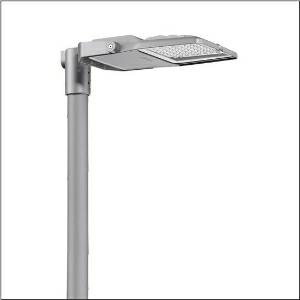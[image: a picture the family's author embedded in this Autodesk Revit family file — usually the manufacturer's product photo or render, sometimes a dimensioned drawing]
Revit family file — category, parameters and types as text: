
# Revit family: floodlight_fl_21_mini___pl33t_5xa7776c2f3a_ca81
name_source: partatom
category: Lighting Fixtures
units: mm (PartAtom-declared; Revit-internal decimal feet)

## family parameters
Cut with Voids When Loaded = No
Host = Face
Light Source = No
Part Type = Normal
Room Calculation Point = No
Round Connector Dimension = Use Diameter
Shared = No

## types (1)
- --- (1 x LED, 12050 lm, 89 W, 3000K)
    Apparent Load = 89 VA
    CIE Flux Codes = 26 75 99 100 100
    Color Rendering = 70
    Color Temperature = 3000K
    Default Elevation = 1800 mm
    Description = Floodlight FL 21 mini, floodlight, primary light control with lens, of PMMA, primary optical cover: protective disc, of toughened safety glass, transparent, light distribution: PL33T, light emission: direct distribution, installation type: surface-mounted, LED, High Power LED, rated luminous flux: 12.050lm, luminous efficacy: 135lm/W, light colour: 730, colour temperature: 3000K, control gear: Smart Interface (Zhaga), control: flexible luminous flux parameterisation, time-dependent luminous flux control, constant luminous flux control, overheat protection, pre-setting: logarithmic dimming characteristic, with terminal, 6-pole, mains connection: 220..240V, AC, 50/60Hz, start of lifetime: 89W, end of service life: 94W, reduction: 43W, luminaire housing, of diecast aluminium, powder-coated, Siteco® metallic grey (DB 702S), corrosivity category C5 mid according to DIN EN ISO 12944, suitable for swimming pools, chlorine-resistant, sealing non-destructively replaceable, please order mast flange separately, mast bracket, of steel, galvanised, powder-coated, Siteco® metallic grey (DB 702S), Smart Interface below and above, protection rating (complete): IP66, insulation class (complete): insulation class II (safety insulation), certification: CE, ENEC, VDE, protection symbol: D, impact resistance: IK08, permissible operating ambient temperature: -40..+40°C, permissible operating ambient temperature for outdoor applications: -40..+50°C, standard: DIN EN 12944, LABS conformity tested according to VDMA 24364:2018-05, packaging unit: 1 piece

Light Distribution: PL33T
    Height = 70 mm
    Lamp = 1 x LED
    Lamp Light Flux = 12050 lm
    Lamp Power = 89 W
    Lamp count = 1
    Length = 485 mm
    Luminous efficacy = 135 lm/W
    Manufacturer = Siteco
    ModVariant = No
    Model = 5XA7776C2F3A
    Number of Poles = 1
    OnlyDefault = Yes
    Power Factor = 1
    Product Name = Floodlight FL 21 mini | PL33T
    Product group = floodlight | pylon annexe
    ProductGroupID = 6201
    Protection Class = Protection class II
    Protection Degree = IP 66
    RLX_Detail_Level = 1
    RLX_Emergency_Light_Flux = 0 lm
    RLX_Emergency_Type = 0
    RLX_Emergency_Type_DB = No
    RlxData = <blob elided: 100885 chars, md5=ad934254>
    Socket = socket
    Standby Power = 0 W
    System Light Flux = 12050 lm
    System Power = 89 W
    Type Comments = factory setting: luminous flux: 100 % | dim-lin: 254 | 456 mA
    Type Image = l_1007125.jpg
    URL = http://relux.com
    VarID = @adj_169911
    Voltage = 0 V
    Weight = 0.00 kg
    Width = 337 mm

## geometry (parser evidence)
native form markers: Blend x4, Sweep x13
no freeform markers — native parametric forms only
